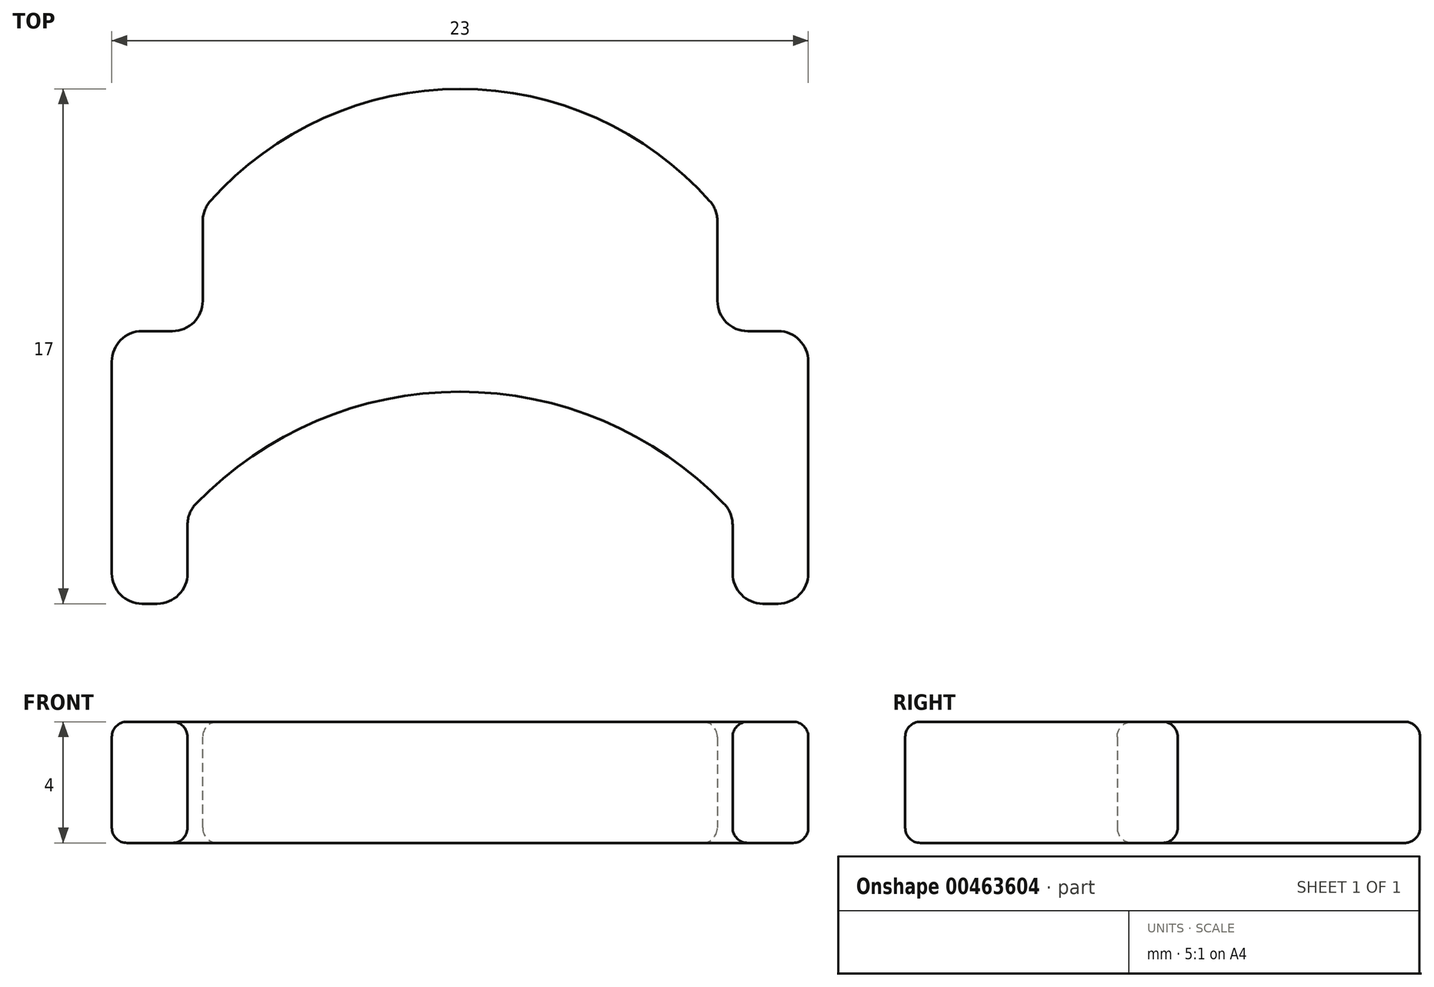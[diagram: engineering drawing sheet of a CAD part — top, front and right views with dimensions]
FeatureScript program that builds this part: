
annotation { "Feature Type Name" : "Feature", "Feature Type Description" : "" }
export const myFeature = defineFeature(function(context is Context, id is Id, definition is map)
    precondition{}
    {
        {
            var Q0;
            Q0=qCreatedBy(makeId("Top.planeOp"),FACE);
            var sketch = newSketch(context, id + "F0", { "sketchPlane" : qUnion([Q0])});
            skLineSegment(sketch, "E0", {"start": v(9, -13) * mm, "end": v(9, -10) * mm});
            skLineSegment(sketch, "E1", {"start": v(-9, -10) * mm, "end": v(-9, -13) * mm});
            skLineSegment(sketch, "E2", {"start": v(-9, -13) * mm, "end": v(-11.5, -13) * mm});
            skLineSegment(sketch, "E3", {"start": v(9, -13) * mm, "end": v(11.5, -13) * mm});
            skLineSegment(sketch, "E4", {"start": v(-11.5, -13) * mm, "end": v(-11.5, -4) * mm});
            skLineSegment(sketch, "E5", {"start": v(-11.5, -4) * mm, "end": v(-8.5, -4) * mm});
            skLineSegment(sketch, "E6", {"start": v(-8.5, -4) * mm, "end": v(-8.5, 0) * mm});
            skLineSegment(sketch, "E7", {"start": v(8.5, 0) * mm, "end": v(8.5, -4) * mm});
            skLineSegment(sketch, "E8", {"start": v(8.5, -4) * mm, "end": v(11.5, -4) * mm});
            skLineSegment(sketch, "E9", {"start": v(11.5, -4) * mm, "end": v(11.5, -13) * mm});
            skLineSegment(sketch, "E10", {"start": v(0, 0) * mm, "end": v(0, 4) * mm});
            skLineSegment(sketch, "E11", {"start": v(0, -10) * mm, "end": v(0, -6) * mm});
            skPoint(sketch, "E11.endSnap0", {"position": v(0, -10) * mm});
            skArc(sketch, "E12", {"start": v(8.5, 0) * mm, "mid": v(0, 4) * mm, "end": v(-8.5, 0) * mm});
            skArc(sketch, "E13", {"start": v(9, -10) * mm, "mid": v(0, -6) * mm, "end": v(-9, -10) * mm});
            skSolve(sketch);
        }
        {
            var Q0;
            Q0=makeQuery(id+"F0.imprint","IMPRINT",FACE,{"disambiguationData":[TD([[makeQuery(id+"F0.imprint","IMPRINT",EDGE,{"derivedFrom":sQuery(id+"F0.wireOp",EDGE,"E0")}),-1.0]])]});
            extrude(context, id + "F1", {"entities" : qUnion([Q0]), "depth" : 4 * mm});
        }
        {
            var Q0;
            Q0=makeQuery(id+"F1.opExtrude","SWEPT_EDGE",EDGE,{"disambiguationData":[OSD([sQuery(id+"F0.wireOp",EDGE,"JVpa2NSN-jCbz-SYZh-2br0-VPJ9OqO5sEDm"),sQuery(id+"F0.wireOp",EDGE,"TmuEh8Bb-qYGH-lmF9-es9h-PXmLGTj7apYS")])]});
            var Q1;
            Q1=makeQuery(id+"F1.opExtrude","SWEPT_EDGE",EDGE,{"disambiguationData":[OSD([sQuery(id+"F0.wireOp",EDGE,"Ta08JTOG-JjW1-DyQu-Rjfl-olB2hLuTZKrI"),sQuery(id+"F0.wireOp",EDGE,"5RLxsvr7-zWRq-nJ0O-23qe-XEgADmnkmLba")])]});
            var Q2;
            Q2=makeQuery(id+"F1.opExtrude","SWEPT_EDGE",EDGE,{"disambiguationData":[OSD([sQuery(id+"F0.wireOp",EDGE,"JVpa2NSN-jCbz-SYZh-2br0-VPJ9OqO5sEDm"),sQuery(id+"F0.wireOp",EDGE,"iIMMWLLX-5pRk-kAWc-YyXh-X3XYjQtiHgF8")])]});
            var Q3;
            Q3=makeQuery(id+"F1.opExtrude","SWEPT_EDGE",EDGE,{"disambiguationData":[OSD([sQuery(id+"F0.wireOp",EDGE,"Bp2VUUx9-f2Nf-Cqm2-FavC-f2X54JljXIIN"),sQuery(id+"F0.wireOp",EDGE,"TmuEh8Bb-qYGH-lmF9-es9h-PXmLGTj7apYS")])]});
            var Q4;
            Q4=makeQuery(id+"F1.opExtrude","SWEPT_EDGE",EDGE,{"disambiguationData":[OSD([sQuery(id+"F0.wireOp",EDGE,"aM0JYdi9-BpOH-c1Sx-eQZ7-4LdQcpM627Qa"),sQuery(id+"F0.wireOp",EDGE,"Ta08JTOG-JjW1-DyQu-Rjfl-olB2hLuTZKrI")])]});
            var Q5;
            Q5=makeQuery(id+"F1.opExtrude","SWEPT_EDGE",EDGE,{"disambiguationData":[OSD([sQuery(id+"F0.wireOp",EDGE,"5RLxsvr7-zWRq-nJ0O-23qe-XEgADmnkmLba"),sQuery(id+"F0.wireOp",EDGE,"Bp2VUUx9-f2Nf-Cqm2-FavC-f2X54JljXIIN")])]});
            var Q6;
            Q6=makeQuery(id+"F1.opExtrude","SWEPT_EDGE",EDGE,{"disambiguationData":[OSD([sQuery(id+"F0.wireOp",EDGE,"yeDMJLls-6pq1-5wso-vwFU-Q73Pk40JU32b"),sQuery(id+"F0.wireOp",EDGE,"aM0JYdi9-BpOH-c1Sx-eQZ7-4LdQcpM627Qa")])]});
            var Q7;
            Q7=makeQuery(id+"F1.opExtrude","SWEPT_EDGE",EDGE,{"disambiguationData":[OSD([sQuery(id+"F0.wireOp",EDGE,"yeDMJLls-6pq1-5wso-vwFU-Q73Pk40JU32b"),sQuery(id+"F0.wireOp",EDGE,"oADVPvip-QRiO-k2je-1GcM-0gCGYZzCVpqe")])]});
            var Q8;
            Q8=makeQuery(id+"F1.opExtrude","SWEPT_EDGE",EDGE,{"disambiguationData":[OSD([sQuery(id+"F0.wireOp",EDGE,"oADVPvip-QRiO-k2je-1GcM-0gCGYZzCVpqe"),sQuery(id+"F0.wireOp",EDGE,"10rlgXVg-n50c-kqx7-uExC-2RYqwfv1c7cX")])]});
            var Q9;
            Q9=makeQuery(id+"F1.opExtrude","SWEPT_EDGE",EDGE,{"disambiguationData":[OSD([sQuery(id+"F0.wireOp",EDGE,"TUznSBm0-cCe5-ovrQ-pSbA-vPagOil4q95r"),sQuery(id+"F0.wireOp",EDGE,"10rlgXVg-n50c-kqx7-uExC-2RYqwfv1c7cX")])]});
            var Q10;
            Q10=makeQuery(id+"F1.opExtrude","SWEPT_EDGE",EDGE,{"disambiguationData":[OSD([sQuery(id+"F0.wireOp",EDGE,"dIuJsfEi-w8Eu-UMFV-xWrQ-Q2fZL97E1xqK"),sQuery(id+"F0.wireOp",EDGE,"TUznSBm0-cCe5-ovrQ-pSbA-vPagOil4q95r")])]});
            var Q11;
            Q11=makeQuery(id+"F1.opExtrude","SWEPT_EDGE",EDGE,{"disambiguationData":[OSD([sQuery(id+"F0.wireOp",EDGE,"iIMMWLLX-5pRk-kAWc-YyXh-X3XYjQtiHgF8"),sQuery(id+"F0.wireOp",EDGE,"dIuJsfEi-w8Eu-UMFV-xWrQ-Q2fZL97E1xqK")])]});
            var Q12;
            Q12=makeQuery(id+"F1.opExtrude","SWEPT_EDGE",EDGE,{"disambiguationData":[OSD([sQuery(id+"F0.wireOp",EDGE,"yLF3BCVI-Jb2U-5dZP-aiB0-7200LCA53yiJ"),sQuery(id+"F0.wireOp",EDGE,"E2")])]});
            var Q13;
            Q13=makeQuery(id+"F1.opExtrude","SWEPT_EDGE",EDGE,{"disambiguationData":[OSD([sQuery(id+"F0.wireOp",EDGE,"E1"),sQuery(id+"F0.wireOp",EDGE,"E2")])]});
            var Q14;
            Q14=makeQuery(id+"F1.opExtrude","SWEPT_EDGE",EDGE,{"disambiguationData":[OSD([sQuery(id+"F0.wireOp",EDGE,"Zq1giByw-Wy4a-OScs-KzMb-DU4RaiEdW2Sl"),sQuery(id+"F0.wireOp",EDGE,"E1")])]});
            var Q15;
            Q15=makeQuery(id+"F1.opExtrude","SWEPT_EDGE",EDGE,{"disambiguationData":[OSD([sQuery(id+"F0.wireOp",EDGE,"E0"),sQuery(id+"F0.wireOp",EDGE,"Zq1giByw-Wy4a-OScs-KzMb-DU4RaiEdW2Sl")])]});
            var Q16;
            Q16=makeQuery(id+"F1.opExtrude","SWEPT_EDGE",EDGE,{"disambiguationData":[OSD([sQuery(id+"F0.wireOp",EDGE,"E0"),sQuery(id+"F0.wireOp",EDGE,"E3")])]});
            var Q17;
            Q17=makeQuery(id+"F1.opExtrude","SWEPT_EDGE",EDGE,{"disambiguationData":[OSD([sQuery(id+"F0.wireOp",EDGE,"W0sLsfjq-YAJu-qSV0-cM3q-n6XLMPe2tytr"),sQuery(id+"F0.wireOp",EDGE,"E3")])]});
            var Q18;
            Q18=makeQuery(id+"F1.opExtrude","SWEPT_EDGE",EDGE,{"disambiguationData":[OSD([sQuery(id+"F0.wireOp",EDGE,"E4"),sQuery(id+"F0.wireOp",EDGE,"E5")])]});
            var Q19;
            Q19=makeQuery(id+"F1.opExtrude","SWEPT_EDGE",EDGE,{"disambiguationData":[OSD([sQuery(id+"F0.wireOp",EDGE,"E5"),sQuery(id+"F0.wireOp",EDGE,"E6")])]});
            var Q20;
            Q20=makeQuery(id+"F1.opExtrude","SWEPT_EDGE",EDGE,{"disambiguationData":[OSD([sQuery(id+"F0.wireOp",EDGE,"E6"),sQuery(id+"F0.wireOp",EDGE,"37HIgoPE-k505-ApNl-kPiv-Fzmli7TXVLkK")])]});
            var Q21;
            Q21=makeQuery(id+"F1.opExtrude","SWEPT_EDGE",EDGE,{"disambiguationData":[OSD([sQuery(id+"F0.wireOp",EDGE,"37HIgoPE-k505-ApNl-kPiv-Fzmli7TXVLkK"),sQuery(id+"F0.wireOp",EDGE,"E7")])]});
            var Q22;
            Q22=makeQuery(id+"F1.opExtrude","SWEPT_EDGE",EDGE,{"disambiguationData":[OSD([sQuery(id+"F0.wireOp",EDGE,"E7"),sQuery(id+"F0.wireOp",EDGE,"E8")])]});
            var Q23;
            Q23=makeQuery(id+"F1.opExtrude","SWEPT_EDGE",EDGE,{"disambiguationData":[OSD([sQuery(id+"F0.wireOp",EDGE,"E8"),sQuery(id+"F0.wireOp",EDGE,"E9")])]});
            fillet(context, id + "F2", {"entities" : qUnion([Q0, Q1, Q2, Q3, Q4, Q5, Q6, Q7, Q8, Q9, Q10, Q11, Q12, Q13, Q14, Q15, Q16, Q17, Q18, Q19, Q20, Q21, Q22, Q23]), "radius" : 1 * mm, "tangentPropagation" : true, "allowEdgeOverflow" : false});
        }
        {
            var Q0;
            Q0=makeQuery(id+"F1.opExtrude","CAP_EDGE",EDGE,{"disambiguationData":[OSD([sQuery(id+"F0.wireOp",EDGE,"10rlgXVg-n50c-kqx7-uExC-2RYqwfv1c7cX")])],"isStart":false});
            var Q1;
            Q1=makeQuery(id+"F1.opExtrude","CAP_EDGE",EDGE,{"disambiguationData":[OSD([sQuery(id+"F0.wireOp",EDGE,"TUznSBm0-cCe5-ovrQ-pSbA-vPagOil4q95r")])],"isStart":true});
            var Q2;
            Q2=makeQuery(id+"F1.opExtrude","CAP_EDGE",EDGE,{"disambiguationData":[OSD([sQuery(id+"F0.wireOp",EDGE,"Zq1giByw-Wy4a-OScs-KzMb-DU4RaiEdW2Sl")])],"isStart":false});
            var Q3;
            Q3=makeQuery(id+"F1.opExtrude","CAP_EDGE",EDGE,{"disambiguationData":[OSD([sQuery(id+"F0.wireOp",EDGE,"E1")])],"isStart":false});
            var Q4;
            Q4=makeQuery(id+"F1.opExtrude","CAP_FACE",FACE,{"disambiguationData":[OSD([sQuery(id+"F0.wireOp",EDGE,"yeDMJLls-6pq1-5wso-vwFU-Q73Pk40JU32b"),sQuery(id+"F0.wireOp",EDGE,"dIuJsfEi-w8Eu-UMFV-xWrQ-Q2fZL97E1xqK"),sQuery(id+"F0.wireOp",EDGE,"TUznSBm0-cCe5-ovrQ-pSbA-vPagOil4q95r"),sQuery(id+"F0.wireOp",EDGE,"oADVPvip-QRiO-k2je-1GcM-0gCGYZzCVpqe"),sQuery(id+"F0.wireOp",EDGE,"10rlgXVg-n50c-kqx7-uExC-2RYqwfv1c7cX"),sQuery(id+"F0.wireOp",EDGE,"yLF3BCVI-Jb2U-5dZP-aiB0-7200LCA53yiJ"),sQuery(id+"F0.wireOp",EDGE,"W0sLsfjq-YAJu-qSV0-cM3q-n6XLMPe2tytr"),sQuery(id+"F0.wireOp",EDGE,"E0"),sQuery(id+"F0.wireOp",EDGE,"Zq1giByw-Wy4a-OScs-KzMb-DU4RaiEdW2Sl"),sQuery(id+"F0.wireOp",EDGE,"E1"),sQuery(id+"F0.wireOp",EDGE,"E2"),sQuery(id+"F0.wireOp",EDGE,"E3")])],"isStart":false});
            var Q5;
            Q5=makeQuery(id+"F1.opExtrude","CAP_EDGE",EDGE,{"disambiguationData":[OSD([sQuery(id+"F0.wireOp",EDGE,"Zq1giByw-Wy4a-OScs-KzMb-DU4RaiEdW2Sl")])],"isStart":true});
            var Q6;
            Q6=makeQuery(id+"F1.opExtrude","CAP_EDGE",EDGE,{"disambiguationData":[OSD([sQuery(id+"F0.wireOp",EDGE,"E3")])],"isStart":true});
            var Q7;
            Q7=makeQuery(id+"F1.opExtrude","CAP_EDGE",EDGE,{"disambiguationData":[OSD([sQuery(id+"F0.wireOp",EDGE,"E0")])],"isStart":true});
            var Q8;
            Q8=makeQuery(id+"F1.opExtrude","CAP_EDGE",EDGE,{"disambiguationData":[OSD([sQuery(id+"F0.wireOp",EDGE,"E1")])],"isStart":true});
            var Q9;
            Q9=makeQuery(id+"F1.opExtrude","CAP_EDGE",EDGE,{"disambiguationData":[OSD([sQuery(id+"F0.wireOp",EDGE,"E2")])],"isStart":true});
            fillet(context, id + "F3", {"entities" : qUnion([Q0, Q1, Q2, Q3, Q4, Q5, Q6, Q7, Q8, Q9]), "radius" : 0.5 * mm, "tangentPropagation" : true, "allowEdgeOverflow" : false});
        }
    });
